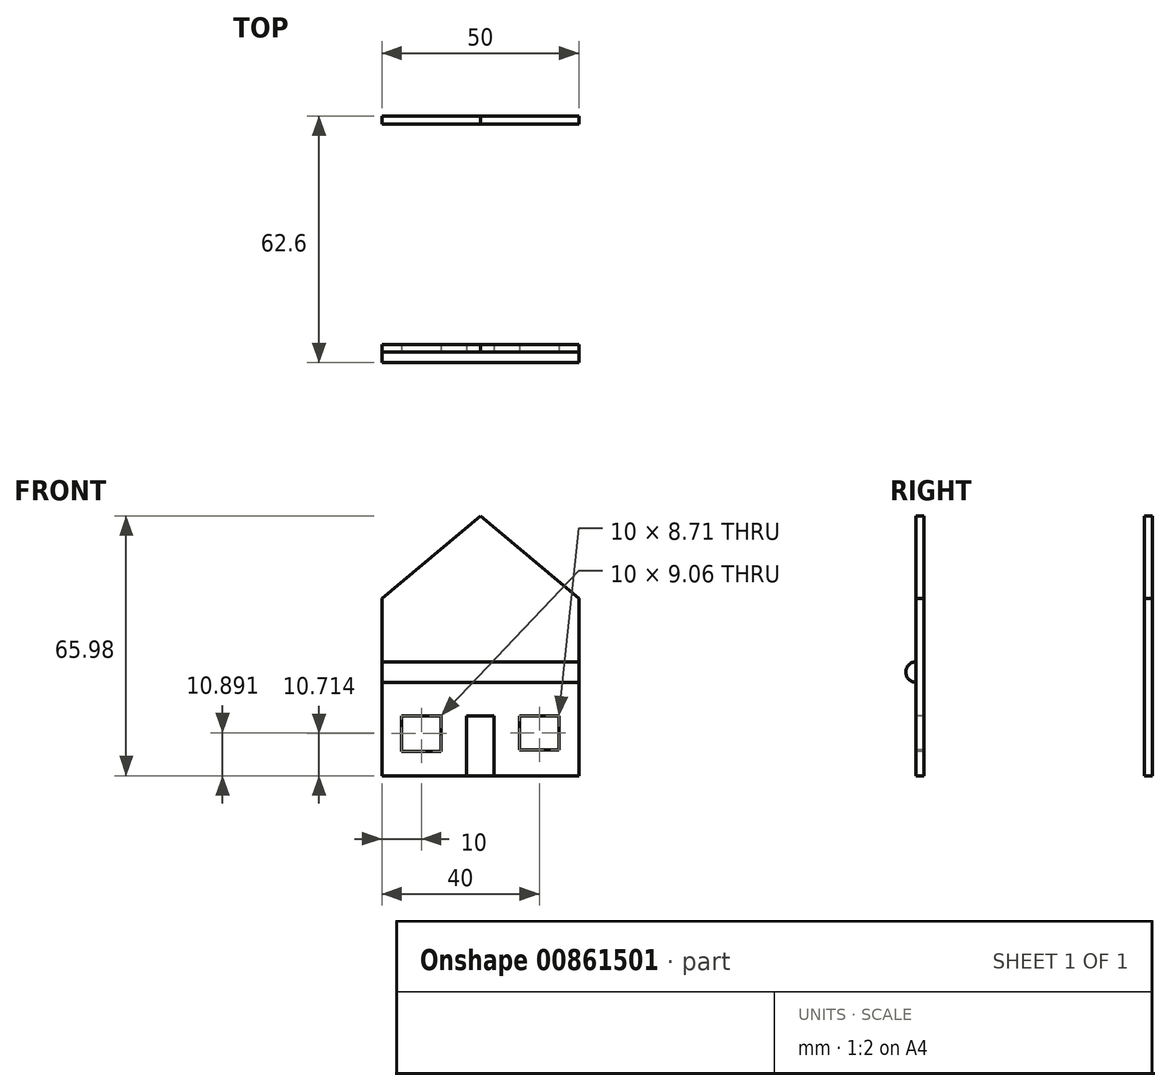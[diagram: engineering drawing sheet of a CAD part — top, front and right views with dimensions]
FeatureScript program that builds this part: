
annotation { "Feature Type Name" : "Feature", "Feature Type Description" : "" }
export const myFeature = defineFeature(function(context is Context, id is Id, definition is map)
    precondition{}
    {
        {
            var Q0;
            Q0=qCreatedBy(makeId("Top.planeOp"),FACE);
            var sketch = newSketch(context, id + "F0", { "sketchPlane" : qUnion([Q0])});
            skLineSegment(sketch, "E0.bottom", {"start": v(0, 0) * mm, "end": v(-50, 0) * mm});
            skLineSegment(sketch, "E0.top", {"start": v(0, 60) * mm, "end": v(-50, 60) * mm});
            skLineSegment(sketch, "E0.left", {"start": v(0, 0) * mm, "end": v(0, 60) * mm});
            skLineSegment(sketch, "E0.right", {"start": v(-50, 0) * mm, "end": v(-50, 60) * mm});
            skLineSegment(sketch, "E1.bottom", {"start": v(-50, 60) * mm, "end": v(-65, 60) * mm});
            skLineSegment(sketch, "E1.top", {"start": v(-50, 30) * mm, "end": v(-65, 30) * mm});
            skLineSegment(sketch, "E1.left", {"start": v(-50, 60) * mm, "end": v(-50, 30) * mm});
            skLineSegment(sketch, "E1.right", {"start": v(-65, 60) * mm, "end": v(-65, 30) * mm});
            skLineSegment(sketch, "E2.0", {"start": v(-2, 58) * mm, "end": v(-48, 58) * mm});
            skLineSegment(sketch, "E2.1", {"start": v(-2, 2) * mm, "end": v(-2, 58) * mm});
            skLineSegment(sketch, "E2.2", {"start": v(-2, 2) * mm, "end": v(-48, 2) * mm});
            skLineSegment(sketch, "E2.3", {"start": v(-48, 2) * mm, "end": v(-48, 58) * mm});
            skLineSegment(sketch, "E3.0", {"start": v(-50, 31) * mm, "end": v(-64, 31) * mm});
            skLineSegment(sketch, "E3.1", {"start": v(-64, 59) * mm, "end": v(-64, 31) * mm});
            skLineSegment(sketch, "E3.2", {"start": v(-50, 59) * mm, "end": v(-64, 59) * mm});
            skSolve(sketch);
        }
        {
            var Q0;
            Q0=qCreatedBy(makeId("Front.planeOp"),FACE);
            var sketch = newSketch(context, id + "F1", { "sketchPlane" : qUnion([Q0])});
            skLineSegment(sketch, "E4", {"start": v(0, 0) * mm, "end": v(0, 45) * mm});
            skLineSegment(sketch, "E5", {"start": v(0, 45) * mm, "end": v(-25, 65.98) * mm});
            skLineSegment(sketch, "E6", {"start": v(-25, 65.98) * mm, "end": v(-50, 45) * mm});
            skLineSegment(sketch, "E7", {"start": v(-50, 45) * mm, "end": v(-50, 0) * mm});
            skLineSegment(sketch, "E8", {"start": v(-50, 0) * mm, "end": v(0, 0) * mm});
            skSolve(sketch);
        }
        {
            var Q0;
            Q0=qCreatedBy(makeId("Front.planeOp"),FACE);
            var Q1;
            Q1=sQuery(id+"F0.wireOp",VERTEX,"E1.top.end");
            cPlane(context, id + "F2", {"entities" : qUnion([Q0, Q1]), "cplaneType" : CPlaneType.PLANE_POINT, "offset" : 25 * mm, "width" : 150 * mm, "height" : 150 * mm});
        }
        {
            var Q0;
            Q0=qCreatedBy(id+"F2.planeOp",FACE);
            var sketch = newSketch(context, id + "F3", { "sketchPlane" : qUnion([Q0])});
            skLineSegment(sketch, "E9", {"start": v(-65, 0) * mm, "end": v(-65, 14.9) * mm});
            skLineSegment(sketch, "E10", {"start": v(-65, 14.9) * mm, "end": v(-50, 23.67) * mm});
            skLineSegment(sketch, "E11", {"start": v(-50, 23.67) * mm, "end": v(-50, 0) * mm});
            skLineSegment(sketch, "E12", {"start": v(-50, 0) * mm, "end": v(-65, 0) * mm});
            skSolve(sketch);
        }
        {
            var Q0;
            Q0=qCreatedBy(makeId("Front.planeOp"),FACE);
            var Q1;
            Q1=sQuery(id+"F0.wireOp",VERTEX,"E0.top.start");
            cPlane(context, id + "F4", {"entities" : qUnion([Q0, Q1]), "cplaneType" : CPlaneType.PLANE_POINT, "offset" : 25 * mm, "width" : 150 * mm, "height" : 150 * mm});
        }
        {
            var Q0;
            Q0=qCreatedBy(id+"F4.planeOp",FACE);
            var sketch = newSketch(context, id + "F5", { "sketchPlane" : qUnion([Q0])});
            skLineSegment(sketch, "E13", {"start": v(0, 0) * mm, "end": v(0, 45) * mm});
            skLineSegment(sketch, "E14", {"start": v(0, 45) * mm, "end": v(-25, 65.98) * mm});
            skLineSegment(sketch, "E15", {"start": v(-25, 65.98) * mm, "end": v(-50, 45) * mm});
            skLineSegment(sketch, "E16", {"start": v(-50, 45) * mm, "end": v(-50, 0) * mm});
            skLineSegment(sketch, "E17", {"start": v(-50, 0) * mm, "end": v(0, 0) * mm});
            skSolve(sketch);
        }
        {
            var Q0;
            Q0 = qSketchRegion(id + "F1", true);
            var Q1;
            Q1=sQuery(id+"F0.wireOp",VERTEX,"E2.1.start");
            extrude(context, id + "F6", {"entities" : qUnion([Q0]), "endBound" : BoundingType.UP_TO_VERTEX, "oppositeDirection" : true, "depth" : 25 * mm, "endBoundEntityVertex" : qUnion([Q1]), "offsetDistance" : 25 * mm});
        }
        {
            var Q0;
            Q0=makeQuery(id+"F5.imprint","IMPRINT",FACE,{"disambiguationData":[TD([[makeQuery(id+"F5.imprint","IMPRINT",EDGE,{"derivedFrom":sQuery(id+"F5.wireOp",EDGE,"E13")}),1.0]])]});
            var Q1;
            Q1=sQuery(id+"F0.wireOp",VERTEX,"E2.0.start");
            extrude(context, id + "F7", {"entities" : qUnion([Q0]), "endBound" : BoundingType.UP_TO_VERTEX, "depth" : 25 * mm, "endBoundEntityVertex" : qUnion([Q1]), "offsetDistance" : 25 * mm});
        }
        {
            var Q0;
            Q0=qCreatedBy(makeId("Front.planeOp"),FACE);
            var sketch = newSketch(context, id + "F8", { "sketchPlane" : qUnion([Q0])});
            skLineSegment(sketch, "E18.bottom", {"start": v(-45, 15.24) * mm, "end": v(-35, 15.24) * mm});
            skLineSegment(sketch, "E18.top", {"start": v(-45, 6.18) * mm, "end": v(-35, 6.18) * mm});
            skLineSegment(sketch, "E18.left", {"start": v(-45, 15.24) * mm, "end": v(-45, 6.18) * mm});
            skLineSegment(sketch, "E18.right", {"start": v(-35, 15.24) * mm, "end": v(-35, 6.18) * mm});
            skLineSegment(sketch, "E19.bottom", {"start": v(-28.5, 0) * mm, "end": v(-21.5, 0) * mm});
            skLineSegment(sketch, "E19.top", {"start": v(-28.5, 15.24) * mm, "end": v(-21.5, 15.24) * mm});
            skLineSegment(sketch, "E19.left", {"start": v(-28.5, 0) * mm, "end": v(-28.5, 15.24) * mm});
            skLineSegment(sketch, "E19.right", {"start": v(-21.5, 0) * mm, "end": v(-21.5, 15.24) * mm});
            skLineSegment(sketch, "E20.bottom", {"start": v(-15, 15.24) * mm, "end": v(-5, 15.24) * mm});
            skLineSegment(sketch, "E20.top", {"start": v(-15, 6.54) * mm, "end": v(-5, 6.54) * mm});
            skLineSegment(sketch, "E20.left", {"start": v(-15, 15.24) * mm, "end": v(-15, 6.54) * mm});
            skLineSegment(sketch, "E20.right", {"start": v(-5, 15.24) * mm, "end": v(-5, 6.54) * mm});
            skLineSegment(sketch, "E21", {"start": v(-25, 65.98) * mm, "end": v(-25, -9.82) * mm, "construction": true});
            skPoint(sketch, "E22", {"position": v(-25, 15.24) * mm});
            skSolve(sketch);
        }
        {
            var Q0;
            Q0 = qSketchRegion(id + "F8", true);
            extrude(context, id + "F9", {"entities" : qUnion([Q0]), "operationType" : NewBodyOperationType.REMOVE, "oppositeDirection" : true, "depth" : 25 * mm, "offsetDistance" : 25 * mm});
        }
        {
            var Q0;
            Q0=qCreatedBy(makeId("Right.planeOp"),FACE);
            var sketch = newSketch(context, id + "F10", { "sketchPlane" : qUnion([Q0])});
            skArc(sketch, "E23", {"start": v(0, 28.91) * mm, "mid": v(-2.6, 26.32) * mm, "end": v(0, 23.72) * mm});
            skLineSegment(sketch, "E24", {"start": v(0, 28.91) * mm, "end": v(0, 23.72) * mm});
            skSolve(sketch);
        }
        {
            var Q0;
            Q0 = qSketchRegion(id + "F10", true);
            var Q1;
            Q1=makeQuery(id+"F10.imprint","IMPRINT",FACE,{"disambiguationData":[TD([[makeQuery(id+"F10.imprint","IMPRINT",EDGE,{"derivedFrom":sQuery(id+"F10.wireOp",EDGE,"E23")}),1.0]])]});
            var Q2;
            Q2=sQuery(id+"F0.wireOp",VERTEX,"E0.bottom.end");
            extrude(context, id + "F11", {"entities" : qUnion([Q0, Q1]), "endBound" : BoundingType.UP_TO_VERTEX, "oppositeDirection" : true, "depth" : 25 * mm, "endBoundEntityVertex" : qUnion([Q2]), "offsetDistance" : 25 * mm});
        }
    });
